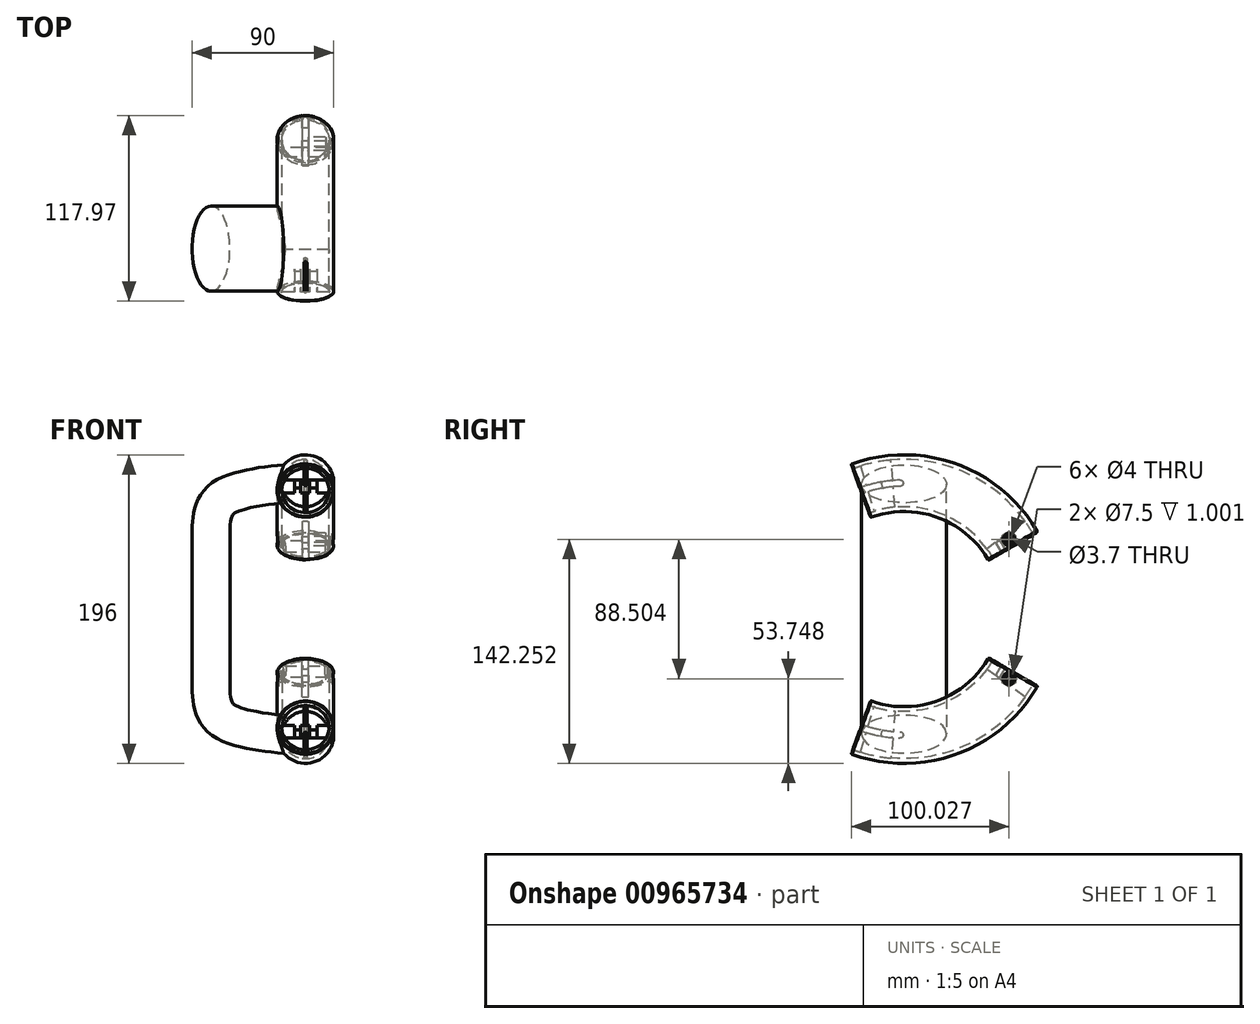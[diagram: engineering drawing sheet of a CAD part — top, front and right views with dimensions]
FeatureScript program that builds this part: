
annotation { "Feature Type Name" : "Feature", "Feature Type Description" : "" }
export const myFeature = defineFeature(function(context is Context, id is Id, definition is map)
    precondition{}
    {
        {
            var Q0;
            Q0=qCreatedBy(makeId("Top.planeOp"),FACE);
            var sketch = newSketch(context, id + "F0", { "sketchPlane" : qUnion([Q0])});
            skEllipse(sketch, "E0", {"center": v(0, 0) * mm, "majorRadius": 27 * mm, "minorRadius": 12 * mm, "majorAxis": v(0, -1)});
            skSolve(sketch);
        }
        {
            var Q0;
            Q0 = qSketchRegion(id + "F0", true);
            extrude(context, id + "F1", {"entities" : qUnion([Q0]), "depth" : 50 * mm, "offsetDistance" : 25 * mm});
        }
        {
            var Q0;
            Q0=makeQuery(id+"F1.opExtrude","CAP_FACE",FACE,{"disambiguationData":[OSD([sQuery(id+"F0.wireOp",EDGE,"E0")])],"isStart":false});
            var sketch = newSketch(context, id + "F2", { "sketchPlane" : qUnion([Q0])});
            skEllipse(sketch, "E1", {"center": v(0, 0) * mm, "majorRadius": 27 * mm, "minorRadius": 12 * mm, "majorAxis": v(0, -1)});
            skSolve(sketch);
        }
        {
            var Q0;
            Q0=qCreatedBy(makeId("Right.planeOp"),FACE);
            cPlane(context, id + "F3", {"entities" : qUnion([Q0]), "cplaneType" : CPlaneType.OFFSET, "offset" : 60 * mm, "width" : 150 * mm, "height" : 150 * mm});
        }
        {
            var Q0;
            Q0=qCreatedBy(makeId("Front.planeOp"),FACE);
            var sketch = newSketch(context, id + "F4", { "sketchPlane" : qUnion([Q0])});
            skFitSpline(sketch, "E2", {"points": [v(0, 50) * mm, v(16.84, 74.59) * mm, v(60, 80) * mm], "startDerivative": vector(0, 112.7) * mm, "endDerivative": vector(72.27, -0.32) * mm});
            skSolve(sketch);
        }
        {
            var Q0;
            Q0 = qSketchRegion(id + "F2", true);
            var Q1;
            Q1 = qConstructionFilter(qBodyType(qCreatedBy(id + "F4" ,EDGE), BodyType.WIRE), ConstructionObject.NO);
            sweep(context, id + "F5", {"operationType" : NewBodyOperationType.ADD, "profiles" : qUnion([Q0]), "path" : qUnion([Q1])});
        }
        {
            var Q0;
            Q0=qCreatedBy(makeId("Front.planeOp"),FACE);
            var sketch = newSketch(context, id + "F6", { "sketchPlane" : qUnion([Q0])});
            skEllipse(sketch, "E3", {"center": v(60, 80) * mm, "majorRadius": 18 * mm, "minorRadius": 18 * mm, "majorAxis": v(1, 0)});
            skSolve(sketch);
        }
        {
            var Q0;
            Q0=qCreatedBy(makeId("Top.planeOp"),FACE);
            var sketch = newSketch(context, id + "F7", { "sketchPlane" : qUnion([Q0])});
            skLineSegment(sketch, "E4", {"start": v(-34.99, 0) * mm, "end": v(93.34, 0) * mm, "construction": true});
            skSolve(sketch);
        }
        {
            var Q0;
            Q0 = qSketchRegion(id + "F6", true);
            var Q1;
            Q1=sQuery(id+"F7.wireOp",EDGE,"E4");
            revolve(context, id + "F8", {"operationType" : NewBodyOperationType.ADD, "surfaceOperationType" : NewSurfaceOperationType.NEW, "entities" : qUnion([Q0]), "axis" : qUnion([Q1]), "revolveType" : RevolveType.TWO_DIRECTIONS, "angle" : 20 * degree, "angleBack" : 300 * degree});
        }
        {
            var Q0;
            Q0=qCreatedBy(makeId("Front.planeOp"),FACE);
            var sketch = newSketch(context, id + "F9", { "sketchPlane" : qUnion([Q0])});
            skCircle(sketch, "E5", {"center": v(60, 80) * mm, "radius": 15 * mm});
            skSolve(sketch);
        }
        {
            var Q0;
            Q0 = qSketchRegion(id + "F9", true);
            var Q1;
            Q1=sQuery(id+"F7.wireOp",EDGE,"E4");
            revolve(context, id + "F10", {"operationType" : NewBodyOperationType.REMOVE, "surfaceOperationType" : NewSurfaceOperationType.NEW, "entities" : qUnion([Q0]), "axis" : qUnion([Q1]), "revolveType" : RevolveType.FULL, "oppositeDirection" : true});
        }
        {
            var Q0;
            Q0=qCreatedBy(id+"F3.planeOp",FACE);
            var sketch = newSketch(context, id + "F11", { "sketchPlane" : qUnion([Q0])});
            skArc(sketch, "E6", {"start": v(-2.56, 81.96) * mm, "mid": v(-14.5, 80.7) * mm, "end": v(-26.11, 77.73) * mm});
            skArc(sketch, "E7", {"start": v(-2.44, 77.96) * mm, "mid": v(-13.78, 76.77) * mm, "end": v(-24.84, 73.94) * mm});
            skArc(sketch, "E8", {"start": v(-26.11, 77.73) * mm, "mid": v(-27.37, 75.2) * mm, "end": v(-24.84, 73.94) * mm});
            skArc(sketch, "E9", {"start": v(-2.44, 77.96) * mm, "mid": v(-0.5, 80.02) * mm, "end": v(-2.56, 81.96) * mm});
            skSolve(sketch);
        }
        {
            var Q0;
            Q0 = qSketchRegion(id + "F11", true);
            extrude(context, id + "F12", {"entities" : qUnion([Q0]), "operationType" : NewBodyOperationType.ADD, "endBound" : BoundingType.SYMMETRIC, "depth" : 34 * mm, "offsetDistance" : 25 * mm});
        }
        {
            var Q0;
            Q0=qCreatedBy(id+"F3.planeOp",FACE);
            cPlane(context, id + "F13", {"entities" : qUnion([Q0]), "cplaneType" : CPlaneType.OFFSET, "offset" : 5 * mm, "width" : 150 * mm, "height" : 150 * mm});
        }
        {
            var Q0;
            Q0=qCreatedBy(id+"F3.planeOp",FACE);
            cPlane(context, id + "F14", {"entities" : qUnion([Q0]), "cplaneType" : CPlaneType.OFFSET, "offset" : 5 * mm, "oppositeDirection" : true, "width" : 150 * mm, "height" : 150 * mm});
        }
        {
            var Q0;
            Q0=qCreatedBy(id+"F13.planeOp",FACE);
            var sketch = newSketch(context, id + "F15", { "sketchPlane" : qUnion([Q0])});
            skArc(sketch, "E10", {"start": v(-15.17, 82.62) * mm, "mid": v(-43.18, 72.05) * mm, "end": v(-65.7, 52.33) * mm});
            skArc(sketch, "E11", {"start": v(-13.4, 74.81) * mm, "mid": v(-39.18, 65.12) * mm, "end": v(-59.83, 46.87) * mm});
            skLineSegment(sketch, "E12", {"start": v(-65.7, 52.33) * mm, "end": v(-59.83, 46.87) * mm});
            skLineSegment(sketch, "E13", {"start": v(-15.17, 82.62) * mm, "end": v(-13.4, 74.81) * mm});
            skSolve(sketch);
        }
        {
            var Q0;
            Q0 = qSketchRegion(id + "F15", true);
            extrude(context, id + "F16", {"entities" : qUnion([Q0]), "operationType" : NewBodyOperationType.REMOVE, "endBound" : BoundingType.SYMMETRIC, "oppositeDirection" : true, "depth" : 5 * mm, "offsetDistance" : 25 * mm});
        }
        {
            var Q0;
            Q0=qCreatedBy(id+"F14.planeOp",FACE);
            var sketch = newSketch(context, id + "F17", { "sketchPlane" : qUnion([Q0])});
            skArc(sketch, "E14", {"start": v(-15.17, 82.62) * mm, "mid": v(-45.1, 70.86) * mm, "end": v(-68.43, 48.72) * mm});
            skArc(sketch, "E15", {"start": v(-13.4, 74.81) * mm, "mid": v(-41.84, 63.44) * mm, "end": v(-63.5, 41.77) * mm});
            skLineSegment(sketch, "E16", {"start": v(-68.43, 48.72) * mm, "end": v(-63.5, 41.77) * mm});
            skLineSegment(sketch, "E17", {"start": v(-15.17, 82.62) * mm, "end": v(-13.4, 74.81) * mm});
            skSolve(sketch);
        }
        {
            var Q0;
            Q0 = qSketchRegion(id + "F17", true);
            extrude(context, id + "F18", {"entities" : qUnion([Q0]), "operationType" : NewBodyOperationType.REMOVE, "endBound" : BoundingType.SYMMETRIC, "oppositeDirection" : true, "depth" : 4 * mm, "offsetDistance" : 25 * mm});
        }
        {
            var Q0;
            Q0=qCreatedBy(makeId("Front.planeOp"),FACE);
            var Q1;
            Q1=sQuery(id+"F7.wireOp",EDGE,"E4");
            cPlane(context, id + "F19", {"entities" : qUnion([Q0, Q1]), "cplaneType" : CPlaneType.LINE_ANGLE, "offset" : 25 * mm, "angle" : 17 * degree, "width" : 150 * mm, "height" : 150 * mm});
        }
        {
            var Q0;
            Q0=qCreatedBy(makeId("Front.planeOp"),FACE);
            var Q1;
            Q1=sQuery(id+"F7.wireOp",EDGE,"E4");
            cPlane(context, id + "F20", {"entities" : qUnion([Q0, Q1]), "cplaneType" : CPlaneType.LINE_ANGLE, "offset" : 25 * mm, "angle" : 60 * degree, "oppositeDirection" : true, "width" : 150 * mm, "height" : 150 * mm});
        }
        {
            var Q0;
            Q0=qCreatedBy(id+"F20.planeOp",FACE);
            var sketch = newSketch(context, id + "F21", { "sketchPlane" : qUnion([Q0])});
            skLineSegment(sketch, "E18.left", {"start": v(62, -94.87) * mm, "end": v(62, -65.13) * mm});
            skLineSegment(sketch, "E18.right", {"start": v(58, -94.87) * mm, "end": v(58, -65.13) * mm});
            skArc(sketch, "E19", {"start": v(62, -65.13) * mm, "mid": v(60, -65) * mm, "end": v(58, -65.13) * mm});
            skArc(sketch, "E20", {"start": v(58, -94.87) * mm, "mid": v(60, -95) * mm, "end": v(62, -94.87) * mm});
            skSolve(sketch);
        }
        {
            var Q0;
            Q0 = qSketchRegion(id + "F21", true);
            var Q1;
            Q1=sQuery(id+"F7.wireOp",EDGE,"E4");
            revolve(context, id + "F22", {"operationType" : NewBodyOperationType.ADD, "surfaceOperationType" : NewSurfaceOperationType.NEW, "entities" : qUnion([Q0]), "axis" : qUnion([Q1]), "revolveType" : RevolveType.ONE_DIRECTION, "angle" : 6 * degree});
        }
        {
            var Q0;
            Q0=makeQuery(id+"F12.boolean.opBoolean","SPLIT",EDGE,{"disambiguationData":[OD(1.0)],"derivedFrom":makeQuery(id+"F10.boolean.opBoolean","INTERSECT",EDGE,{"derivedFrom":[makeQuery(id+"F8.opRevolve","CAP_FACE",FACE,{"disambiguationData":[OSD([sQuery(id+"F6.wireOp",EDGE,"E3")])],"isStart":false}),makeQuery(id+"F10.opRevolve","SWEPT_FACE",FACE,{"disambiguationData":[OSD([sQuery(id+"F9.wireOp",EDGE,"E5")])]})]})});
            var Q1;
            Q1=makeQuery(id+"F12.boolean.opBoolean","SPLIT",EDGE,{"disambiguationData":[OD(0.0)],"derivedFrom":makeQuery(id+"F10.boolean.opBoolean","INTERSECT",EDGE,{"derivedFrom":[makeQuery(id+"F8.opRevolve","CAP_FACE",FACE,{"disambiguationData":[OSD([sQuery(id+"F6.wireOp",EDGE,"E3")])],"isStart":false}),makeQuery(id+"F10.opRevolve","SWEPT_FACE",FACE,{"disambiguationData":[OSD([sQuery(id+"F9.wireOp",EDGE,"E5")])]})]})});
            var Q2;
            Q2=makeQuery(id+"F8.opRevolve","CAP_EDGE",EDGE,{"disambiguationData":[OSD([sQuery(id+"F6.wireOp",EDGE,"E3")])],"isStart":false});
            fillet(context, id + "F23", {"entities" : qUnion([Q0, Q1, Q2]), "radius" : 0.5 * mm, "tangentPropagation" : true, "allowEdgeOverflow" : false});
        }
        {
            var Q0;
            Q0=qCreatedBy(id+"F19.planeOp",FACE);
            var sketch = newSketch(context, id + "F24", { "sketchPlane" : qUnion([Q0])});
            skLineSegment(sketch, "E21.bottom", {"start": v(-59, 96) * mm, "end": v(-61, 96) * mm});
            skLineSegment(sketch, "E21.top", {"start": v(-59, 63) * mm, "end": v(-61, 63) * mm});
            skLineSegment(sketch, "E21.left", {"start": v(-59, 96) * mm, "end": v(-59, 63) * mm});
            skLineSegment(sketch, "E21.right", {"start": v(-61, 96) * mm, "end": v(-61, 63) * mm});
            skSolve(sketch);
        }
        {
            var Q0;
            Q0 = qSketchRegion(id + "F24", true);
            var Q1;
            Q1=sQuery(id+"F7.wireOp",EDGE,"E4");
            revolve(context, id + "F25", {"operationType" : NewBodyOperationType.ADD, "surfaceOperationType" : NewSurfaceOperationType.NEW, "entities" : qUnion([Q0]), "axis" : qUnion([Q1]), "revolveType" : RevolveType.ONE_DIRECTION, "oppositeDirection" : true, "angle" : 12 * degree});
        }
        {
            var Q0;
            {var subQ0=sQuery(id+"F24.wireOp",EDGE,"E21.right");var subQ1=sQuery(id+"F15.wireOp",EDGE,"E13");var subQ2=sQuery(id+"F15.wireOp",EDGE,"E12");var subQ3=sQuery(id+"F15.wireOp",EDGE,"E11");var subQ4=sQuery(id+"F15.wireOp",EDGE,"E10");var subQ5=makeQuery(id+"F16.opExtrude","CAP_FACE",FACE,{"disambiguationData":[OSD([subQ4,subQ3,subQ2,subQ1])],"isStart":false});var subQ6=sQuery(id+"F11.wireOp",EDGE,"E6");Q0=makeQuery(id+"F25.boolean.opBoolean","SPLIT",EDGE,{"disambiguationData":[TD([makeQuery(id+"FeQc5akP4JFHVbd_1.opFillet","BLEND_FACE",FACE,{"disambiguationData":[OSD([subQ6,subQ4,subQ3,subQ2,subQ1]),TDD([makeQuery(id+"F16.boolean.opBoolean","INTERSECT",EDGE,{"derivedFrom":[makeQuery(id+"F12.opExtrude","SWEPT_FACE",FACE,{"disambiguationData":[OSD([subQ6])]}),subQ5]})])]})])],"derivedFrom":makeQuery(id+"F25.opRevolve","CAP_EDGE",EDGE,{"disambiguationData":[OSD([subQ0])],"isStart":true})});}
            var Q1;
            {var subQ0=sQuery(id+"F17.wireOp",EDGE,"E17");var subQ1=sQuery(id+"F17.wireOp",EDGE,"E16");var subQ2=sQuery(id+"F17.wireOp",EDGE,"E15");var subQ3=sQuery(id+"F17.wireOp",EDGE,"E14");var subQ4=makeQuery(id+"F18.opExtrude","CAP_FACE",FACE,{"disambiguationData":[OSD([subQ3,subQ2,subQ1,subQ0])],"isStart":true});var subQ5=sQuery(id+"F11.wireOp",EDGE,"E6");var subQ6=sQuery(id+"F24.wireOp",EDGE,"E21.left");Q1=makeQuery(id+"F25.boolean.opBoolean","SPLIT",EDGE,{"disambiguationData":[TD([makeQuery(id+"FeQc5akP4JFHVbd_1.opFillet","BLEND_FACE",FACE,{"disambiguationData":[OSD([subQ5,subQ3,subQ2,subQ1,subQ0]),TDD([makeQuery(id+"F18.boolean.opBoolean","INTERSECT",EDGE,{"derivedFrom":[makeQuery(id+"F12.opExtrude","SWEPT_FACE",FACE,{"disambiguationData":[OSD([subQ5])]}),subQ4]})])]})])],"derivedFrom":makeQuery(id+"F25.opRevolve","CAP_EDGE",EDGE,{"disambiguationData":[OSD([subQ6])],"isStart":true})});}
            var Q2;
            {var subQ0=sQuery(id+"F24.wireOp",EDGE,"E21.right");var subQ1=sQuery(id+"F15.wireOp",EDGE,"E13");var subQ2=sQuery(id+"F15.wireOp",EDGE,"E12");var subQ3=sQuery(id+"F15.wireOp",EDGE,"E11");var subQ4=sQuery(id+"F15.wireOp",EDGE,"E10");var subQ5=makeQuery(id+"F16.opExtrude","CAP_FACE",FACE,{"disambiguationData":[OSD([subQ4,subQ3,subQ2,subQ1])],"isStart":false});var subQ6=sQuery(id+"F11.wireOp",EDGE,"E7");Q2=makeQuery(id+"F25.boolean.opBoolean","SPLIT",EDGE,{"disambiguationData":[TD([makeQuery(id+"FeQc5akP4JFHVbd_1.opFillet","BLEND_FACE",FACE,{"disambiguationData":[OSD([subQ6,subQ4,subQ3,subQ2,subQ1]),TDD([makeQuery(id+"F16.boolean.opBoolean","INTERSECT",EDGE,{"derivedFrom":[makeQuery(id+"F12.opExtrude","SWEPT_FACE",FACE,{"disambiguationData":[OSD([subQ6])]}),subQ5]})])]})])],"derivedFrom":makeQuery(id+"F25.opRevolve","CAP_EDGE",EDGE,{"disambiguationData":[OSD([subQ0])],"isStart":true})});}
            var Q3;
            {var subQ0=sQuery(id+"F17.wireOp",EDGE,"E17");var subQ1=sQuery(id+"F17.wireOp",EDGE,"E16");var subQ2=sQuery(id+"F17.wireOp",EDGE,"E15");var subQ3=sQuery(id+"F17.wireOp",EDGE,"E14");var subQ4=makeQuery(id+"F18.opExtrude","CAP_FACE",FACE,{"disambiguationData":[OSD([subQ3,subQ2,subQ1,subQ0])],"isStart":true});var subQ5=sQuery(id+"F11.wireOp",EDGE,"E7");var subQ6=sQuery(id+"F24.wireOp",EDGE,"E21.left");Q3=makeQuery(id+"F25.boolean.opBoolean","SPLIT",EDGE,{"disambiguationData":[TD([makeQuery(id+"FeQc5akP4JFHVbd_1.opFillet","BLEND_FACE",FACE,{"disambiguationData":[OSD([subQ5,subQ3,subQ2,subQ1,subQ0]),TDD([makeQuery(id+"F18.boolean.opBoolean","INTERSECT",EDGE,{"derivedFrom":[makeQuery(id+"F12.opExtrude","SWEPT_FACE",FACE,{"disambiguationData":[OSD([subQ5])]}),subQ4]})])]})])],"derivedFrom":makeQuery(id+"F25.opRevolve","CAP_EDGE",EDGE,{"disambiguationData":[OSD([subQ6])],"isStart":true})});}
            var Q4;
            {var subQ0=sQuery(id+"F24.wireOp",EDGE,"E21.right");Q4=makeQuery(id+"F25.boolean.opBoolean","SPLIT",EDGE,{"disambiguationData":[TD([makeQuery(id+"F12.opExtrude","SWEPT_FACE",FACE,{"disambiguationData":[OSD([sQuery(id+"F11.wireOp",EDGE,"E6")])]})])],"derivedFrom":makeQuery(id+"F25.opRevolve","CAP_EDGE",EDGE,{"disambiguationData":[OSD([subQ0])],"isStart":false})});}
            var Q5;
            {var subQ0=sQuery(id+"F24.wireOp",EDGE,"E21.right");Q5=makeQuery(id+"F25.boolean.opBoolean","SPLIT",EDGE,{"disambiguationData":[TD([makeQuery(id+"F12.opExtrude","SWEPT_FACE",FACE,{"disambiguationData":[OSD([sQuery(id+"F11.wireOp",EDGE,"E7")])]})])],"derivedFrom":makeQuery(id+"F25.opRevolve","CAP_EDGE",EDGE,{"disambiguationData":[OSD([subQ0])],"isStart":false})});}
            var Q6;
            {var subQ0=sQuery(id+"F24.wireOp",EDGE,"E21.left");Q6=makeQuery(id+"F25.boolean.opBoolean","SPLIT",EDGE,{"disambiguationData":[TD([makeQuery(id+"F12.opExtrude","SWEPT_FACE",FACE,{"disambiguationData":[OSD([sQuery(id+"F11.wireOp",EDGE,"E6")])]})])],"derivedFrom":makeQuery(id+"F25.opRevolve","CAP_EDGE",EDGE,{"disambiguationData":[OSD([subQ0])],"isStart":false})});}
            var Q7;
            {var subQ0=sQuery(id+"F24.wireOp",EDGE,"E21.left");Q7=makeQuery(id+"F25.boolean.opBoolean","SPLIT",EDGE,{"disambiguationData":[TD([makeQuery(id+"F12.opExtrude","SWEPT_FACE",FACE,{"disambiguationData":[OSD([sQuery(id+"F11.wireOp",EDGE,"E7")])]})])],"derivedFrom":makeQuery(id+"F25.opRevolve","CAP_EDGE",EDGE,{"disambiguationData":[OSD([subQ0])],"isStart":false})});}
            fillet(context, id + "F26", {"entities" : qUnion([Q0, Q1, Q2, Q3, Q4, Q5, Q6, Q7]), "radius" : 1 * mm, "tangentPropagation" : true, "allowEdgeOverflow" : false});
        }
        {
            var Q0;
            Q0=qCreatedBy(id+"F3.planeOp",FACE);
            var sketch = newSketch(context, id + "F27", { "sketchPlane" : qUnion([Q0])});
            skCircle(sketch, "E22", {"center": v(66.65, 44.25) * mm, "radius": 2 * mm});
            skSolve(sketch);
        }
        {
            var Q0;
            Q0 = qSketchRegion(id + "F27", true);
            extrude(context, id + "F28", {"entities" : qUnion([Q0]), "operationType" : NewBodyOperationType.REMOVE, "endBound" : BoundingType.SYMMETRIC, "oppositeDirection" : true, "depth" : 40 * mm, "offsetDistance" : 25 * mm});
        }
        {
            var Q0;
            Q0=qCreatedBy(id+"F3.planeOp",FACE);
            cPlane(context, id + "F29", {"entities" : qUnion([Q0]), "cplaneType" : CPlaneType.OFFSET, "offset" : 18 * mm, "width" : 150 * mm, "height" : 150 * mm});
        }
        {
            var Q0;
            Q0=qCreatedBy(id+"F29.planeOp",FACE);
            var sketch = newSketch(context, id + "F30", { "sketchPlane" : qUnion([Q0])});
            skCircle(sketch, "E23", {"center": v(66.65, 44.25) * mm, "radius": 3.75 * mm});
            skSolve(sketch);
        }
        {
            var Q0;
            Q0 = qSketchRegion(id + "F30", true);
            extrude(context, id + "F31", {"entities" : qUnion([Q0]), "operationType" : NewBodyOperationType.REMOVE, "oppositeDirection" : true, "depth" : 1 * mm, "offsetDistance" : 25 * mm});
        }
        {
            var Q0;
            Q0=qCreatedBy(id+"F3.planeOp",FACE);
            cPlane(context, id + "F32", {"entities" : qUnion([Q0]), "cplaneType" : CPlaneType.OFFSET, "offset" : 18 * mm, "oppositeDirection" : true, "width" : 150 * mm, "height" : 150 * mm});
        }
        {
            var Q0;
            Q0=qCreatedBy(id+"F32.planeOp",FACE);
            var sketch = newSketch(context, id + "F33", { "sketchPlane" : qUnion([Q0])});
            skLineSegment(sketch, "E24", {"start": v(66.65, 49.15) * mm, "end": v(70.9, 46.7) * mm});
            skLineSegment(sketch, "E25", {"start": v(70.9, 46.7) * mm, "end": v(70.9, 41.79) * mm});
            skLineSegment(sketch, "E26", {"start": v(70.9, 41.79) * mm, "end": v(66.65, 39.34) * mm});
            skLineSegment(sketch, "E27", {"start": v(66.65, 39.34) * mm, "end": v(62.4, 41.78) * mm});
            skLineSegment(sketch, "E28", {"start": v(62.4, 41.78) * mm, "end": v(62.4, 46.7) * mm});
            skLineSegment(sketch, "E29", {"start": v(62.4, 46.7) * mm, "end": v(66.65, 49.15) * mm});
            skSolve(sketch);
        }
        {
            var Q0;
            Q0 = qSketchRegion(id + "F33", true);
            extrude(context, id + "F34", {"entities" : qUnion([Q0]), "operationType" : NewBodyOperationType.REMOVE, "depth" : 1 * mm, "offsetDistance" : 25 * mm});
        }
        {
            var Q0;
            Q0=makeQuery(id+"F22.opRevolve","CAP_EDGE",EDGE,{"disambiguationData":[OSD([sQuery(id+"F21.wireOp",EDGE,"E18.left")])],"isStart":true});
            var Q1;
            Q1=makeQuery(id+"F22.opRevolve","CAP_EDGE",EDGE,{"disambiguationData":[OSD([sQuery(id+"F21.wireOp",EDGE,"E18.right")])],"isStart":true});
            var Q2;
            {var subQ0=makeQuery(id+"F8.opRevolve","CAP_FACE",FACE,{"disambiguationData":[OSD([sQuery(id+"F6.wireOp",EDGE,"E3")])],"isStart":true});var subQ1=sQuery(id+"F21.wireOp",EDGE,"E18.left");var subQ2=makeQuery(id+"F10.opRevolve","SWEPT_FACE",FACE,{"disambiguationData":[OSD([sQuery(id+"F9.wireOp",EDGE,"E5")])]});Q2=makeQuery(id+"F22.boolean.opBoolean","SPLIT",EDGE,{"disambiguationData":[TD([makeQuery(id+"F22.opRevolve","SWEPT_FACE",FACE,{"disambiguationData":[OSD([subQ1])]})])],"derivedFrom":makeQuery(id+"F10.boolean.opBoolean","INTERSECT",EDGE,{"derivedFrom":[subQ0,subQ2]})});}
            var Q3;
            {var subQ0=makeQuery(id+"F8.opRevolve","CAP_FACE",FACE,{"disambiguationData":[OSD([sQuery(id+"F6.wireOp",EDGE,"E3")])],"isStart":true});var subQ1=makeQuery(id+"F10.opRevolve","SWEPT_FACE",FACE,{"disambiguationData":[OSD([sQuery(id+"F9.wireOp",EDGE,"E5")])]});var subQ2=sQuery(id+"F21.wireOp",EDGE,"E18.right");Q3=makeQuery(id+"F22.boolean.opBoolean","SPLIT",EDGE,{"disambiguationData":[TD([makeQuery(id+"F22.opRevolve","SWEPT_FACE",FACE,{"disambiguationData":[OSD([subQ2])]})])],"derivedFrom":makeQuery(id+"F10.boolean.opBoolean","INTERSECT",EDGE,{"derivedFrom":[subQ0,subQ1]})});}
            var Q4;
            Q4=makeQuery(id+"F8.opRevolve","CAP_EDGE",EDGE,{"disambiguationData":[OSD([sQuery(id+"F6.wireOp",EDGE,"E3")])],"isStart":true});
            fillet(context, id + "F35", {"entities" : qUnion([Q0, Q1, Q2, Q3, Q4]), "radius" : .75 * mm, "tangentPropagation" : true, "allowEdgeOverflow" : false});
        }
        {
            var Q0;
            Q0=qCreatedBy(id+"F20.planeOp",FACE);
            var sketch = newSketch(context, id + "F36", { "sketchPlane" : qUnion([Q0])});
            skArc(sketch, "E30", {"start": v(75.02, -74.5) * mm, "mid": v(74.37, -72.96) * mm, "end": v(73.56, -71.5) * mm});
            skLineSegment(sketch, "E31", {"start": v(75.02, -74.5) * mm, "end": v(44.98, -74.5) * mm});
            skLineSegment(sketch, "E32", {"start": v(73.56, -71.5) * mm, "end": v(46.44, -71.5) * mm});
            skArc(sketch, "E33.trimOffspring", {"start": v(46.44, -71.5) * mm, "mid": v(45.63, -72.96) * mm, "end": v(44.98, -74.5) * mm});
            skSolve(sketch);
        }
        {
            var Q0;
            Q0 = qSketchRegion(id + "F36", true);
            extrude(context, id + "F37", {"entities" : qUnion([Q0]), "operationType" : NewBodyOperationType.ADD, "oppositeDirection" : true, "depth" : 7.5 * mm, "offsetDistance" : 25 * mm});
        }
        {
            var Q0;
            Q0=makeQuery(id+"F16.boolean.opBoolean","INTERSECT",EDGE,{"derivedFrom":[makeQuery(id+"F12.opExtrude","SWEPT_FACE",FACE,{"disambiguationData":[OSD([sQuery(id+"F11.wireOp",EDGE,"E6")])]}),makeQuery(id+"F16.opExtrude","SWEPT_FACE",FACE,{"disambiguationData":[OSD([sQuery(id+"F15.wireOp",EDGE,"E13")])]})]});
            var Q1;
            Q1=makeQuery(id+"F16.boolean.opBoolean","INTERSECT",EDGE,{"derivedFrom":[makeQuery(id+"F12.opExtrude","SWEPT_FACE",FACE,{"disambiguationData":[OSD([sQuery(id+"F11.wireOp",EDGE,"E7")])]}),makeQuery(id+"F16.opExtrude","SWEPT_FACE",FACE,{"disambiguationData":[OSD([sQuery(id+"F15.wireOp",EDGE,"E13")])]})]});
            var Q2;
            Q2=makeQuery(id+"F18.boolean.opBoolean","INTERSECT",EDGE,{"derivedFrom":[makeQuery(id+"F12.opExtrude","SWEPT_FACE",FACE,{"disambiguationData":[OSD([sQuery(id+"F11.wireOp",EDGE,"E6")])]}),makeQuery(id+"F18.opExtrude","SWEPT_FACE",FACE,{"disambiguationData":[OSD([sQuery(id+"F17.wireOp",EDGE,"E17")])]})]});
            var Q3;
            Q3=makeQuery(id+"F18.boolean.opBoolean","INTERSECT",EDGE,{"derivedFrom":[makeQuery(id+"F12.opExtrude","SWEPT_FACE",FACE,{"disambiguationData":[OSD([sQuery(id+"F11.wireOp",EDGE,"E7")])]}),makeQuery(id+"F18.opExtrude","SWEPT_FACE",FACE,{"disambiguationData":[OSD([sQuery(id+"F17.wireOp",EDGE,"E17")])]})]});
            var Q4;
            {var subQ1=sQuery(id+"F24.wireOp",EDGE,"E21.right");var subQ5=makeQuery(id+"F12.opExtrude","SWEPT_FACE",FACE,{"disambiguationData":[OSD([sQuery(id+"F11.wireOp",EDGE,"E6")])]});var subQ7=makeQuery(id+"F25.opRevolve","SWEPT_FACE",FACE,{"disambiguationData":[OSD([subQ1])]});Q4=makeQuery(id+"F26.opFillet","BLEND_EDGE",EDGE,{"blendedFrom":[makeQuery(id+"F25.boolean.opBoolean","SPLIT",EDGE,{"disambiguationData":[TD([subQ5])],"derivedFrom":makeQuery(id+"F25.opRevolve","CAP_EDGE",EDGE,{"disambiguationData":[OSD([subQ1])],"isStart":false})}),makeQuery(id+"F25.boolean.opBoolean","SPLIT",FACE,{"disambiguationData":[TD([subQ5])],"derivedFrom":subQ7})],"blendedInto":[makeQuery(id+"F25.boolean.opBoolean","SPLIT",FACE,{"disambiguationData":[TD([subQ5])],"derivedFrom":subQ7})]});}
            var Q5;
            {var subQ0=sQuery(id+"F24.wireOp",EDGE,"E21.right");Q5=makeQuery(id+"F25.boolean.opBoolean","SPLIT",EDGE,{"disambiguationData":[TD([makeQuery(id+"F12.opExtrude","SWEPT_FACE",FACE,{"disambiguationData":[OSD([sQuery(id+"F11.wireOp",EDGE,"E6")])]})])],"derivedFrom":makeQuery(id+"F25.opRevolve","CAP_EDGE",EDGE,{"disambiguationData":[OSD([subQ0])],"isStart":true})});}
            var Q6;
            {var subQ0=sQuery(id+"F24.wireOp",EDGE,"E21.left");Q6=makeQuery(id+"F25.boolean.opBoolean","SPLIT",EDGE,{"disambiguationData":[TD([makeQuery(id+"F12.opExtrude","SWEPT_FACE",FACE,{"disambiguationData":[OSD([sQuery(id+"F11.wireOp",EDGE,"E6")])]})])],"derivedFrom":makeQuery(id+"F25.opRevolve","CAP_EDGE",EDGE,{"disambiguationData":[OSD([subQ0])],"isStart":true})});}
            var Q7;
            {var subQ0=sQuery(id+"F24.wireOp",EDGE,"E21.right");Q7=makeQuery(id+"F25.boolean.opBoolean","SPLIT",EDGE,{"disambiguationData":[TD([makeQuery(id+"F12.opExtrude","SWEPT_FACE",FACE,{"disambiguationData":[OSD([sQuery(id+"F11.wireOp",EDGE,"E7")])]})])],"derivedFrom":makeQuery(id+"F25.opRevolve","CAP_EDGE",EDGE,{"disambiguationData":[OSD([subQ0])],"isStart":true})});}
            var Q8;
            {var subQ2=sQuery(id+"F24.wireOp",EDGE,"E21.left");var subQ5=makeQuery(id+"F12.opExtrude","SWEPT_FACE",FACE,{"disambiguationData":[OSD([sQuery(id+"F11.wireOp",EDGE,"E6")])]});var subQ7=makeQuery(id+"F25.opRevolve","SWEPT_FACE",FACE,{"disambiguationData":[OSD([subQ2])]});Q8=makeQuery(id+"F26.opFillet","BLEND_EDGE",EDGE,{"blendedFrom":[makeQuery(id+"F25.boolean.opBoolean","SPLIT",EDGE,{"disambiguationData":[TD([subQ5])],"derivedFrom":makeQuery(id+"F25.opRevolve","CAP_EDGE",EDGE,{"disambiguationData":[OSD([subQ2])],"isStart":false})}),makeQuery(id+"F25.boolean.opBoolean","SPLIT",FACE,{"disambiguationData":[TD([subQ5])],"derivedFrom":subQ7})],"blendedInto":[makeQuery(id+"F25.boolean.opBoolean","SPLIT",FACE,{"disambiguationData":[TD([subQ5])],"derivedFrom":subQ7})]});}
            var Q9;
            {var subQ2=sQuery(id+"F24.wireOp",EDGE,"E21.left");var subQ5=makeQuery(id+"F12.opExtrude","SWEPT_FACE",FACE,{"disambiguationData":[OSD([sQuery(id+"F11.wireOp",EDGE,"E7")])]});var subQ7=makeQuery(id+"F25.opRevolve","SWEPT_FACE",FACE,{"disambiguationData":[OSD([subQ2])]});Q9=makeQuery(id+"F26.opFillet","BLEND_EDGE",EDGE,{"blendedFrom":[makeQuery(id+"F25.boolean.opBoolean","SPLIT",EDGE,{"disambiguationData":[TD([subQ5])],"derivedFrom":makeQuery(id+"F25.opRevolve","CAP_EDGE",EDGE,{"disambiguationData":[OSD([subQ2])],"isStart":false})}),makeQuery(id+"F25.boolean.opBoolean","SPLIT",FACE,{"disambiguationData":[TD([subQ5])],"derivedFrom":subQ7})],"blendedInto":[makeQuery(id+"F25.boolean.opBoolean","SPLIT",FACE,{"disambiguationData":[TD([subQ5])],"derivedFrom":subQ7})]});}
            var Q10;
            {var subQ0=sQuery(id+"F24.wireOp",EDGE,"E21.left");Q10=makeQuery(id+"F25.boolean.opBoolean","SPLIT",EDGE,{"disambiguationData":[TD([makeQuery(id+"F12.opExtrude","SWEPT_FACE",FACE,{"disambiguationData":[OSD([sQuery(id+"F11.wireOp",EDGE,"E7")])]})])],"derivedFrom":makeQuery(id+"F25.opRevolve","CAP_EDGE",EDGE,{"disambiguationData":[OSD([subQ0])],"isStart":true})});}
            var Q11;
            {var subQ1=sQuery(id+"F24.wireOp",EDGE,"E21.right");var subQ5=makeQuery(id+"F12.opExtrude","SWEPT_FACE",FACE,{"disambiguationData":[OSD([sQuery(id+"F11.wireOp",EDGE,"E7")])]});var subQ7=makeQuery(id+"F25.opRevolve","SWEPT_FACE",FACE,{"disambiguationData":[OSD([subQ1])]});Q11=makeQuery(id+"F26.opFillet","BLEND_EDGE",EDGE,{"blendedFrom":[makeQuery(id+"F25.boolean.opBoolean","SPLIT",EDGE,{"disambiguationData":[TD([subQ5])],"derivedFrom":makeQuery(id+"F25.opRevolve","CAP_EDGE",EDGE,{"disambiguationData":[OSD([subQ1])],"isStart":false})}),makeQuery(id+"F25.boolean.opBoolean","SPLIT",FACE,{"disambiguationData":[TD([subQ5])],"derivedFrom":subQ7})],"blendedInto":[makeQuery(id+"F25.boolean.opBoolean","SPLIT",FACE,{"disambiguationData":[TD([subQ5])],"derivedFrom":subQ7})]});}
            fillet(context, id + "F38", {"entities" : qUnion([Q0, Q1, Q2, Q3, Q4, Q5, Q6, Q7, Q8, Q9, Q10, Q11]), "radius" : 1 * mm, "tangentPropagation" : true, "allowEdgeOverflow" : false});
        }
        {
            var Q0;
            {var subQ4=sQuery(id+"F21.wireOp",EDGE,"E18.left");var subQ6=sQuery(id+"F36.wireOp",EDGE,"E31");Q0=makeQuery(id+"F37.boolean.opBoolean","SPLIT",EDGE,{"disambiguationData":[TD([makeQuery(id+"F35.opFillet","BLEND_FACE",FACE,{"disambiguationData":[OSD([subQ4])]})])],"derivedFrom":makeQuery(id+"F37.opExtrude","CAP_EDGE",EDGE,{"disambiguationData":[OSD([subQ6])],"isStart":true})});}
            var Q1;
            {var subQ4=sQuery(id+"F21.wireOp",EDGE,"E18.left");var subQ6=sQuery(id+"F36.wireOp",EDGE,"E32");Q1=makeQuery(id+"F37.boolean.opBoolean","SPLIT",EDGE,{"disambiguationData":[TD([makeQuery(id+"F35.opFillet","BLEND_FACE",FACE,{"disambiguationData":[OSD([subQ4])]})])],"derivedFrom":makeQuery(id+"F37.opExtrude","CAP_EDGE",EDGE,{"disambiguationData":[OSD([subQ6])],"isStart":true})});}
            var Q2;
            {var subQ0=sQuery(id+"F21.wireOp",EDGE,"E18.right");var subQ1=sQuery(id+"F36.wireOp",EDGE,"E32");Q2=makeQuery(id+"F37.boolean.opBoolean","SPLIT",EDGE,{"disambiguationData":[TD([makeQuery(id+"F35.opFillet","BLEND_FACE",FACE,{"disambiguationData":[OSD([subQ0])]})])],"derivedFrom":makeQuery(id+"F37.opExtrude","CAP_EDGE",EDGE,{"disambiguationData":[OSD([subQ1])],"isStart":true})});}
            var Q3;
            {var subQ0=sQuery(id+"F21.wireOp",EDGE,"E18.right");var subQ1=sQuery(id+"F36.wireOp",EDGE,"E31");Q3=makeQuery(id+"F37.boolean.opBoolean","SPLIT",EDGE,{"disambiguationData":[TD([makeQuery(id+"F35.opFillet","BLEND_FACE",FACE,{"disambiguationData":[OSD([subQ0])]})])],"derivedFrom":makeQuery(id+"F37.opExtrude","CAP_EDGE",EDGE,{"disambiguationData":[OSD([subQ1])],"isStart":true})});}
            var Q4;
            {var subQ0=sQuery(id+"F36.wireOp",EDGE,"E31");Q4=makeQuery(id+"F37.boolean.opBoolean","SPLIT",EDGE,{"disambiguationData":[TD([makeQuery(id+"F22.opRevolve","SWEPT_FACE",FACE,{"disambiguationData":[OSD([sQuery(id+"F21.wireOp",EDGE,"E18.right")])]})])],"derivedFrom":makeQuery(id+"F37.opExtrude","CAP_EDGE",EDGE,{"disambiguationData":[OSD([subQ0])],"isStart":false})});}
            var Q5;
            {var subQ0=sQuery(id+"F36.wireOp",EDGE,"E31");Q5=makeQuery(id+"F37.boolean.opBoolean","SPLIT",EDGE,{"disambiguationData":[TD([makeQuery(id+"F22.opRevolve","SWEPT_FACE",FACE,{"disambiguationData":[OSD([sQuery(id+"F21.wireOp",EDGE,"E18.left")])]})])],"derivedFrom":makeQuery(id+"F37.opExtrude","CAP_EDGE",EDGE,{"disambiguationData":[OSD([subQ0])],"isStart":false})});}
            var Q6;
            {var subQ0=sQuery(id+"F36.wireOp",EDGE,"E32");Q6=makeQuery(id+"F37.boolean.opBoolean","SPLIT",EDGE,{"disambiguationData":[TD([makeQuery(id+"F22.opRevolve","SWEPT_FACE",FACE,{"disambiguationData":[OSD([sQuery(id+"F21.wireOp",EDGE,"E18.right")])]})])],"derivedFrom":makeQuery(id+"F37.opExtrude","CAP_EDGE",EDGE,{"disambiguationData":[OSD([subQ0])],"isStart":false})});}
            var Q7;
            {var subQ0=sQuery(id+"F36.wireOp",EDGE,"E32");Q7=makeQuery(id+"F37.boolean.opBoolean","SPLIT",EDGE,{"disambiguationData":[TD([makeQuery(id+"F22.opRevolve","SWEPT_FACE",FACE,{"disambiguationData":[OSD([sQuery(id+"F21.wireOp",EDGE,"E18.left")])]})])],"derivedFrom":makeQuery(id+"F37.opExtrude","CAP_EDGE",EDGE,{"disambiguationData":[OSD([subQ0])],"isStart":false})});}
            fillet(context, id + "F39", {"entities" : qUnion([Q0, Q1, Q2, Q3, Q4, Q5, Q6, Q7]), "radius" : 1 * mm, "tangentPropagation" : true, "allowEdgeOverflow" : false});
        }
        {
            var Q0;
            Q0=makeQuery(id+"F1.opExtrude","SWEPT_BODY",BODY,{"disambiguationData":[OSD([sQuery(id+"F0.wireOp",EDGE,"E0")])]});
            var Q1;
            Q1=qCreatedBy(makeId("Top.planeOp"),FACE);
            mirror(context, id + "F40", {"operationType" : NewBodyOperationType.ADD, "entities" : qUnion([Q0]), "mirrorPlane" : qUnion([Q1])});
        }
        {
            var Q0;
            Q0=makeQuery(id+"F22.opRevolve","SWEPT_FACE",FACE,{"disambiguationData":[OSD([sQuery(id+"F21.wireOp",EDGE,"E18.left")])]});
            var sketch = newSketch(context, id + "F41", { "sketchPlane" : qUnion([Q0])});
            skCircle(sketch, "E34", {"center": v(66.65, 44.25) * mm, "radius": 1.85 * mm});
            skCircle(sketch, "E35", {"center": v(66.65, 44.25) * mm, "radius": 4.18 * mm});
            skSolve(sketch);
        }
        {
            var Q0;
            Q0 = qSketchRegion(id + "F41", true);
            extrude(context, id + "F42", {"entities" : qUnion([Q0]), "depth" : 11 * mm, "offsetDistance" : 25 * mm});
        }
        {
            var Q0;
            Q0=makeQuery(id+"F42.opExtrude","CAP_EDGE",EDGE,{"disambiguationData":[OSD([sQuery(id+"F41.wireOp",EDGE,"E35")])],"isStart":false});
            fillet(context, id + "F43", {"entities" : qUnion([Q0]), "radius" : .5 * mm, "tangentPropagation" : true, "allowEdgeOverflow" : false});
        }
    });
